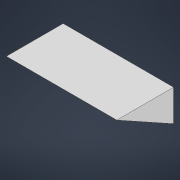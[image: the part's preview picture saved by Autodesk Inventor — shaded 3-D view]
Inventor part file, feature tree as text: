
AUTODESK INVENTOR PART (.ipt)
format: ipt  version: 2022 (Build 260153000, 153)  size: 103,936 bytes
history: native  units: in
note: dims shown in document units (in); Inventor stores cm internally (conversion verified against a paired STEP export)
features: extrude x3, sketch x3
ambient origin geometry x8: Origin, YZ Plane, XZ Plane, XY Plane, X Axis, Y Axis, Z Axis, Center Point
bodies: Solid1 (feature_tree)
feature tree (6):
  extrude  "Extrusion1"  Depth=13.7795in
  extrude  "Extrusion2"  TaperAngle=0.0deg  [1 undecoded]
  extrude  "Extrusion3"  TaperAngle=0.0deg  [1 undecoded]
  sketch  "Sketch1"  dims[d0=13.7795in d1=3.937in]
  sketch  "Sketch2"  dims[d2=7.0866in d3=0.0in d5=0.0in d6=0.0in]
  sketch  "Sketch3"  dims[d8=0.3937in d9=0.0in d10=0.0in d4=0.0197in]
note: 2 required parameter values undecoded (feature->parameter linkage not recoverable at this tier; creation-order binding heuristic only, values carry confidence <= 0.55)
